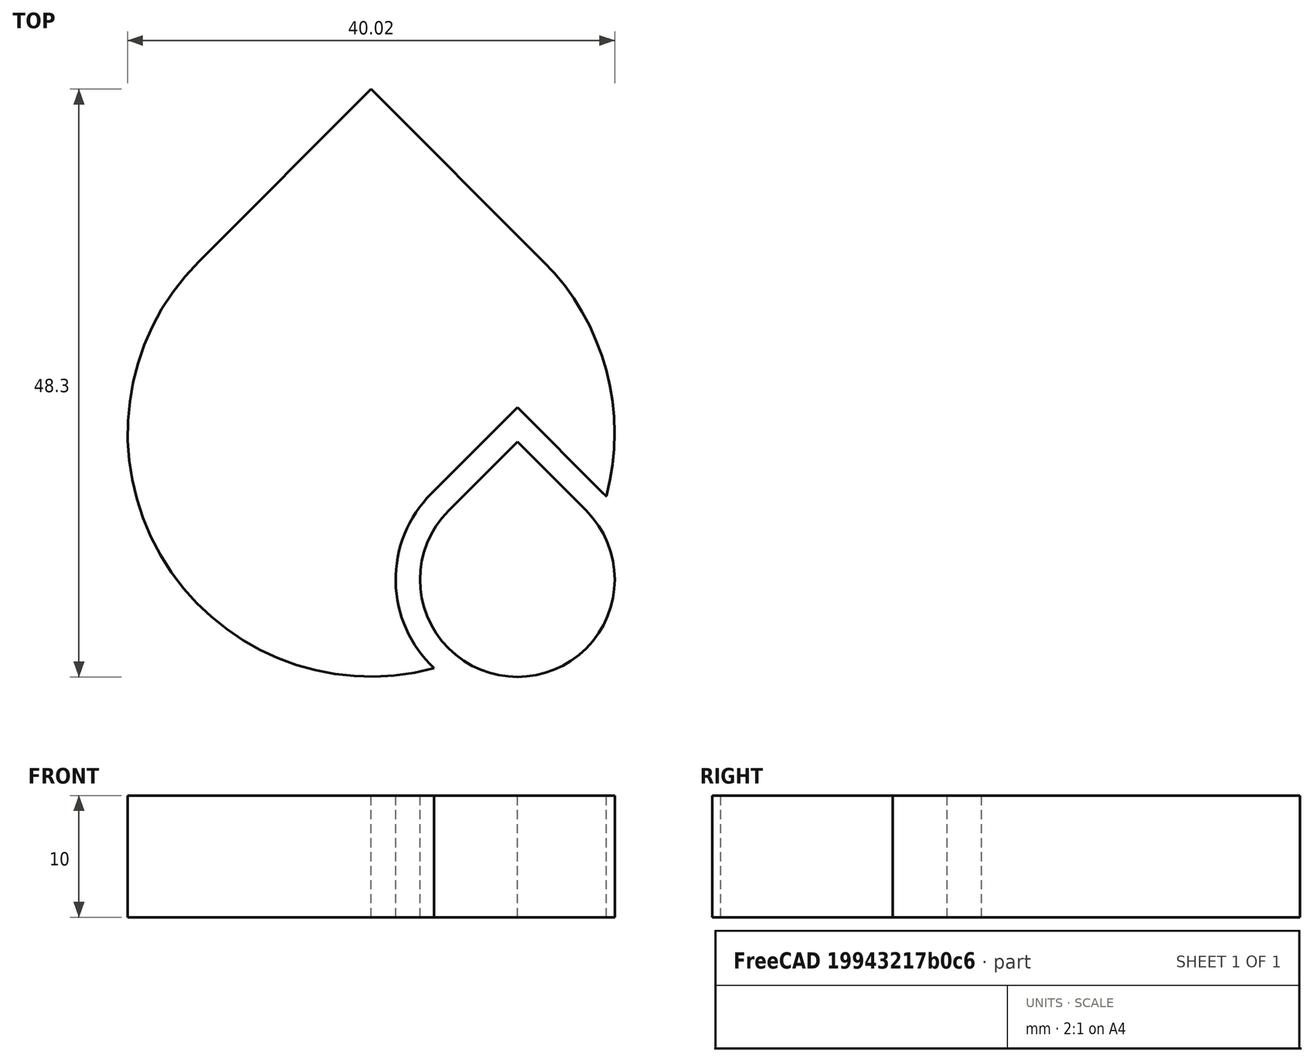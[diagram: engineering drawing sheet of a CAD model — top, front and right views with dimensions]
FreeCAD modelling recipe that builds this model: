
FCSTD DOCUMENT  (FreeCAD 0.16R6703 (Git))
Label: rrl-logo
License: All rights reserved
LicenseURL: http://en.wikipedia.org/wiki/All_rights_reserved
objects: Part::Cylinder×3, Part::Box×3, Part::Fuse×3, Part::MultiFuse×1, Part::Cut×1
note: 11 computed .brp shape members not serialized (recipe doc carries the construction recipe); baked Part::Feature solids carry a one-line shape summary decoded from their .brp

FEATURE [Part::Cylinder] Cylinder
  Angle = 360
  Height = 10
  Radius = 20
FEATURE [Part::Box] Box  label="Cube"
  Height = 10
  Length = 20
  Placement = pos=(0,-20,0) rot=(0,0,1;0rad)
  Width = 20
FEATURE [Part::Fuse] Fusion
  Base = -> Cylinder
  Tool = -> Box
FEATURE [Part::Cylinder] Cylinder001
  Angle = 360
  Height = 12
  Placement = pos=(0,0,-1) rot=(0,0,1;0rad)
  Radius = 10
FEATURE [Part::Box] Box001  label="Cube001"
  Height = 12
  Length = 10
  Placement = pos=(0,-10,-1) rot=(0,0,1;0rad)
  Width = 10
FEATURE [Part::Fuse] Fusion001
  Base = -> Cylinder001
  Placement = pos=(-17,0,0) rot=(0,0,1;0rad)
  Tool = -> Box001
FEATURE [Part::Cylinder] Cylinder002
  Angle = 360
  Height = 10
  Radius = 8
FEATURE [Part::Box] Box003  label="Cube003"
  Height = 10
  Length = 8
  Placement = pos=(0,-8,0) rot=(0,0,1;0rad)
  Width = 8
FEATURE [Part::MultiFuse] Fusion002
  Placement = pos=(-17,0,0) rot=(0,0,1;0rad)
  Shapes = -> [Cylinder002,Box003]
FEATURE [Part::Cut] Cut
  Base = -> Fusion
  Tool = -> Fusion001
FEATURE [Part::Fuse] Fusion003  label="rrl-logo"
  Base = -> Fusion002
  Placement = pos=(0,0,0) rot=(0,0,1;2.35619rad)
  Tool = -> Cut
